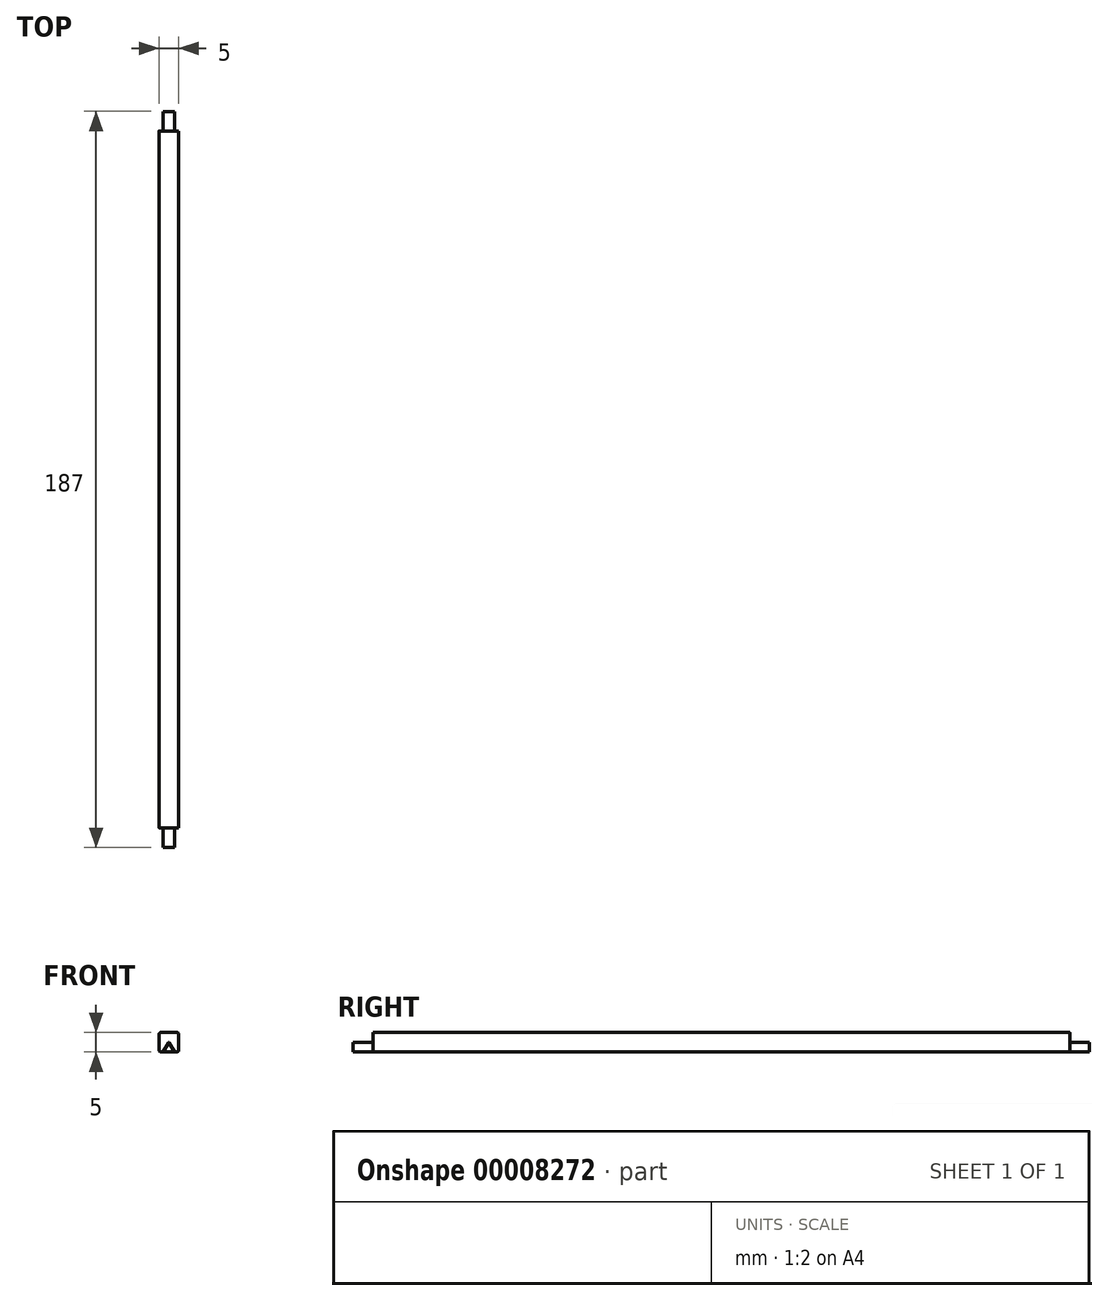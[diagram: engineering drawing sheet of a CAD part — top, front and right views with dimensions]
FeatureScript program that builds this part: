
annotation { "Feature Type Name" : "Feature", "Feature Type Description" : "" }
export const myFeature = defineFeature(function(context is Context, id is Id, definition is map)
    precondition{}
    {
        {
            var Q0;
            Q0=qCreatedBy(makeId("Top.planeOp"),FACE);
            var sketch = newSketch(context, id + "F0", { "sketchPlane" : qUnion([Q0])});
            skLineSegment(sketch, "E0.bottom", {"start": v(-34.8, 166.92) * mm, "end": v(-29.8, 166.92) * mm});
            skLineSegment(sketch, "E0.top", {"start": v(-34.8, -20.08) * mm, "end": v(-29.8, -20.08) * mm});
            skLineSegment(sketch, "E0.left", {"start": v(-34.8, 166.92) * mm, "end": v(-34.8, -20.08) * mm});
            skLineSegment(sketch, "E0.right", {"start": v(-29.8, 166.92) * mm, "end": v(-29.8, -20.08) * mm});
            skSolve(sketch);
        }
        {
            var Q0;
            Q0=qSketchRegion(id+"F0",true);
            extrude(context, id + "F1", {"entities" : qUnion([Q0]), "depth" : 5 * mm});
        }
        {
            var Q0;
            Q0=makeQuery(id+"F1.opExtrude","SWEPT_FACE",FACE,{"disambiguationData":[OSD([sQuery(id+"F0.wireOp",EDGE,"E0.top")])]});
            var sketch = newSketch(context, id + "F2", { "sketchPlane" : qUnion([Q0])});
            skLineSegment(sketch, "E1", {"start": v(-30.84, 0) * mm, "end": v(-32.3, 2.51) * mm});
            skLineSegment(sketch, "E2", {"start": v(-32.3, 2.51) * mm, "end": v(-33.74, 0) * mm});
            skLineSegment(sketch, "E3", {"start": v(-32.3, 2.51) * mm, "end": v(-29.8, 2.51) * mm, "construction": true});
            skLineSegment(sketch, "E4", {"start": v(-32.3, 2.51) * mm, "end": v(-34.8, 2.51) * mm, "construction": true});
            skLineSegment(sketch, "E5.bottom", {"start": v(-34.8, 5) * mm, "end": v(-29.8, 5) * mm});
            skLineSegment(sketch, "E5.top", {"start": v(-34.8, 0) * mm, "end": v(-33.74, 0) * mm});
            skLineSegment(sketch, "E5.left", {"start": v(-34.8, 5) * mm, "end": v(-34.8, 0) * mm});
            skLineSegment(sketch, "E5.right", {"start": v(-29.8, 5) * mm, "end": v(-29.8, 0) * mm});
            skLineSegment(sketch, "E6.trimOffspring", {"start": v(-30.84, 0) * mm, "end": v(-29.8, 0) * mm});
            skSolve(sketch);
        }
        {
            var Q0;
            Q0=qSketchRegion(id+"F2",true);
            extrude(context, id + "F3", {"entities" : qUnion([Q0]), "operationType" : NewBodyOperationType.REMOVE, "oppositeDirection" : true, "depth" : 5 * mm});
        }
        {
            var Q0;
            Q0=makeQuery(id+"F1.opExtrude","SWEPT_FACE",FACE,{"disambiguationData":[OSD([sQuery(id+"F0.wireOp",EDGE,"E0.bottom")])]});
            var sketch = newSketch(context, id + "F4", { "sketchPlane" : qUnion([Q0])});
            skLineSegment(sketch, "E7", {"start": v(32.3, 2.51) * mm, "end": v(33.74, 0) * mm});
            skLineSegment(sketch, "E8", {"start": v(30.84, 0) * mm, "end": v(32.3, 2.51) * mm});
            skLineSegment(sketch, "E9.bottom", {"start": v(29.8, 5) * mm, "end": v(34.8, 5) * mm});
            skLineSegment(sketch, "E9.top", {"start": v(29.8, 0) * mm, "end": v(30.84, 0) * mm});
            skLineSegment(sketch, "E9.left", {"start": v(29.8, 5) * mm, "end": v(29.8, 0) * mm});
            skLineSegment(sketch, "E9.right", {"start": v(34.8, 5) * mm, "end": v(34.8, 0) * mm});
            skLineSegment(sketch, "E10.trimOffspring", {"start": v(33.74, 0) * mm, "end": v(34.8, 0) * mm});
            skSolve(sketch);
        }
        {
            var Q0;
            Q0=qSketchRegion(id+"F4",true);
            extrude(context, id + "F5", {"entities" : qUnion([Q0]), "operationType" : NewBodyOperationType.REMOVE, "oppositeDirection" : true, "depth" : 5 * mm});
        }
        {
            var Q0;
            Q0=makeQuery(id+"F3.boolean.opBoolean","COPY",EDGE,{"derivedFrom":makeQuery(id+"F3.opExtrude","SWEPT_EDGE",EDGE,{"disambiguationData":[OSD([sQuery(id+"F2.wireOp",EDGE,"E1"),sQuery(id+"F2.wireOp",EDGE,"E2")])]})});
            var Q1;
            Q1=makeQuery(id+"F3.boolean.opBoolean","COPY",EDGE,{"derivedFrom":makeQuery(id+"F3.opExtrude","SWEPT_EDGE",EDGE,{"disambiguationData":[OSD([sQuery(id+"F0.wireOp",EDGE,"E0.top"),sQuery(id+"F2.wireOp",EDGE,"E1"),sQuery(id+"F2.wireOp",EDGE,"E6.trimOffspring")])]})});
            var Q2;
            Q2=makeQuery(id+"F3.boolean.opBoolean","COPY",EDGE,{"derivedFrom":makeQuery(id+"F3.opExtrude","SWEPT_EDGE",EDGE,{"disambiguationData":[OSD([sQuery(id+"F0.wireOp",EDGE,"E0.top"),sQuery(id+"F2.wireOp",EDGE,"E2"),sQuery(id+"F2.wireOp",EDGE,"E5.top")])]})});
            var Q3;
            Q3=makeQuery(id+"F5.boolean.opBoolean","COPY",EDGE,{"derivedFrom":makeQuery(id+"F5.opExtrude","SWEPT_EDGE",EDGE,{"disambiguationData":[OSD([sQuery(id+"F4.wireOp",EDGE,"E7"),sQuery(id+"F4.wireOp",EDGE,"E8")])]})});
            var Q4;
            Q4=makeQuery(id+"F5.boolean.opBoolean","COPY",EDGE,{"derivedFrom":makeQuery(id+"F5.opExtrude","SWEPT_EDGE",EDGE,{"disambiguationData":[OSD([sQuery(id+"F0.wireOp",EDGE,"E0.bottom"),sQuery(id+"F4.wireOp",EDGE,"E7"),sQuery(id+"F4.wireOp",EDGE,"E10.trimOffspring")])]})});
            var Q5;
            Q5=makeQuery(id+"F5.boolean.opBoolean","COPY",EDGE,{"derivedFrom":makeQuery(id+"F5.opExtrude","SWEPT_EDGE",EDGE,{"disambiguationData":[OSD([sQuery(id+"F0.wireOp",EDGE,"E0.bottom"),sQuery(id+"F4.wireOp",EDGE,"E8"),sQuery(id+"F4.wireOp",EDGE,"E9.top")])]})});
            fillet(context, id + "F6", {"entities" : qUnion([Q0, Q1, Q2, Q3, Q4, Q5]), "radius" : 0.1 * mm, "tangentPropagation" : true, "allowEdgeOverflow" : false});
        }
        {
            var Q0;
            Q0=makeQuery(id+"F1.opExtrude","CAP_EDGE",EDGE,{"disambiguationData":[OSD([sQuery(id+"F0.wireOp",EDGE,"E0.left")])],"isStart":false});
            var Q1;
            Q1=makeQuery(id+"F1.opExtrude","CAP_EDGE",EDGE,{"disambiguationData":[OSD([sQuery(id+"F0.wireOp",EDGE,"E0.right")])],"isStart":false});
            var Q2;
            Q2=makeQuery(id+"F1.opExtrude","CAP_EDGE",EDGE,{"disambiguationData":[OSD([sQuery(id+"F0.wireOp",EDGE,"E0.right")])],"isStart":true});
            var Q3;
            Q3=makeQuery(id+"F1.opExtrude","CAP_EDGE",EDGE,{"disambiguationData":[OSD([sQuery(id+"F0.wireOp",EDGE,"E0.left")])],"isStart":true});
            fillet(context, id + "F7", {"entities" : qUnion([Q0, Q1, Q2, Q3]), "radius" : 0.5 * mm, "tangentPropagation" : true, "allowEdgeOverflow" : false});
        }
    });
